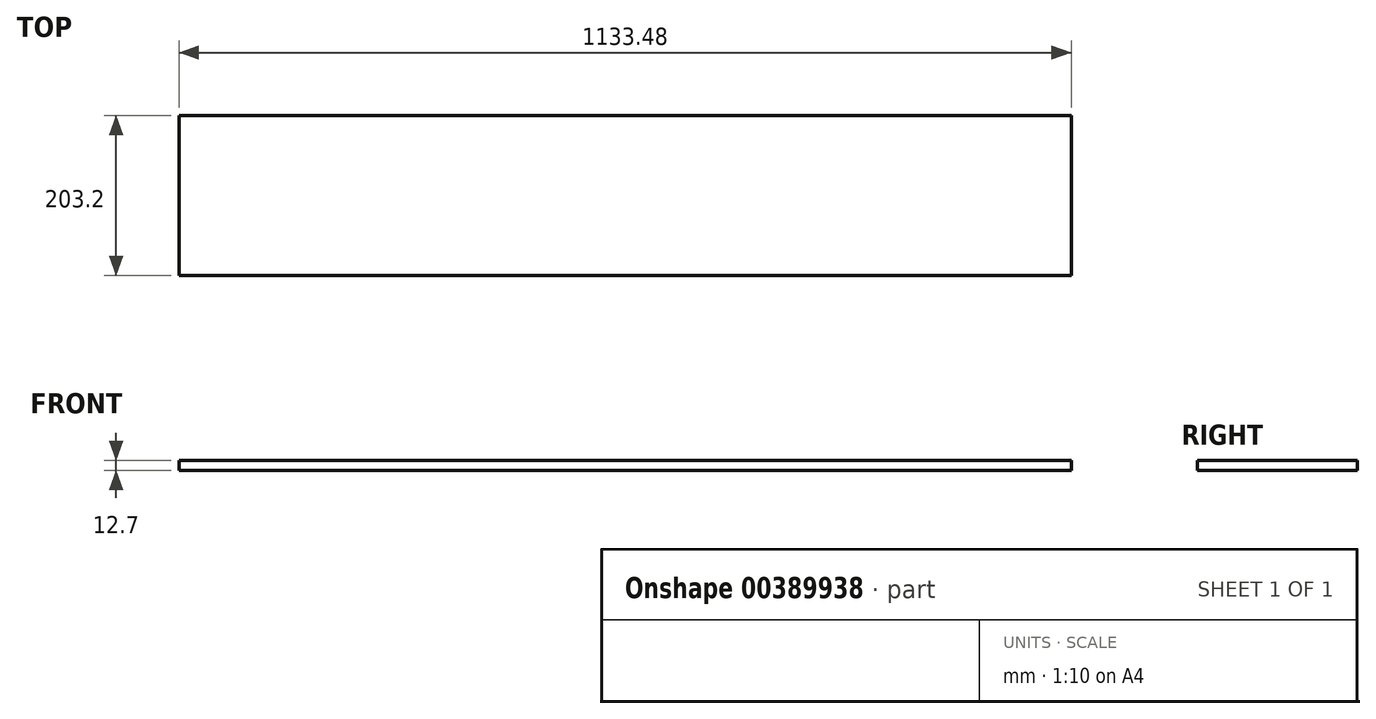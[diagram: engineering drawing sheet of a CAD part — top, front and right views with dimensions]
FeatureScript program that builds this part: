
annotation { "Feature Type Name" : "Feature", "Feature Type Description" : "" }
export const myFeature = defineFeature(function(context is Context, id is Id, definition is map)
    precondition{}
    {
        {
            var Q0;
            Q0=qCreatedBy(makeId("Top.planeOp"),FACE);
            var sketch = newSketch(context, id + "F0", { "sketchPlane" : qUnion([Q0])});
            skLineSegment(sketch, "E0.bottom", {"start": v(566.74, -101.6) * mm, "end": v(-566.74, -101.6) * mm});
            skLineSegment(sketch, "E0.top", {"start": v(566.74, 101.6) * mm, "end": v(-566.74, 101.6) * mm});
            skLineSegment(sketch, "E0.left", {"start": v(566.74, -101.6) * mm, "end": v(566.74, 101.6) * mm});
            skLineSegment(sketch, "E0.right", {"start": v(-566.74, -101.6) * mm, "end": v(-566.74, 101.6) * mm});
            skPoint(sketch, "E0.middle", {"position": v(0, 0) * mm});
            skSolve(sketch);
        }
        {
            var Q0;
            Q0 = qSketchRegion(id + "F0", true);
            extrude(context, id + "F1", {"entities" : qUnion([Q0]), "depth" : 12.7 * mm});
        }
    });
